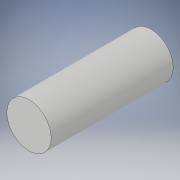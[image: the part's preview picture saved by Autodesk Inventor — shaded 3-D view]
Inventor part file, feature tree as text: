
AUTODESK INVENTOR PART (.ipt)
format: ipt  version: 2019 (Build 230136000, 136)  size: 89,088 bytes
history: native  units: in
note: dims shown in document units (in); Inventor stores cm internally (conversion verified against a paired STEP export)
features: extrude x1, sketch x1
ambient origin geometry x8: Origin, YZ Plane, XZ Plane, XY Plane, X Axis, Y Axis, Z Axis, Center Point
bodies: Solid1 (feature_tree)
feature tree (2):
  extrude  "Extrusion1"  Depth=0.38in TaperAngle=0.0deg
  sketch  "Sketch1"  dims[d0=0.138in d1=0.38in d2=0.0in]
